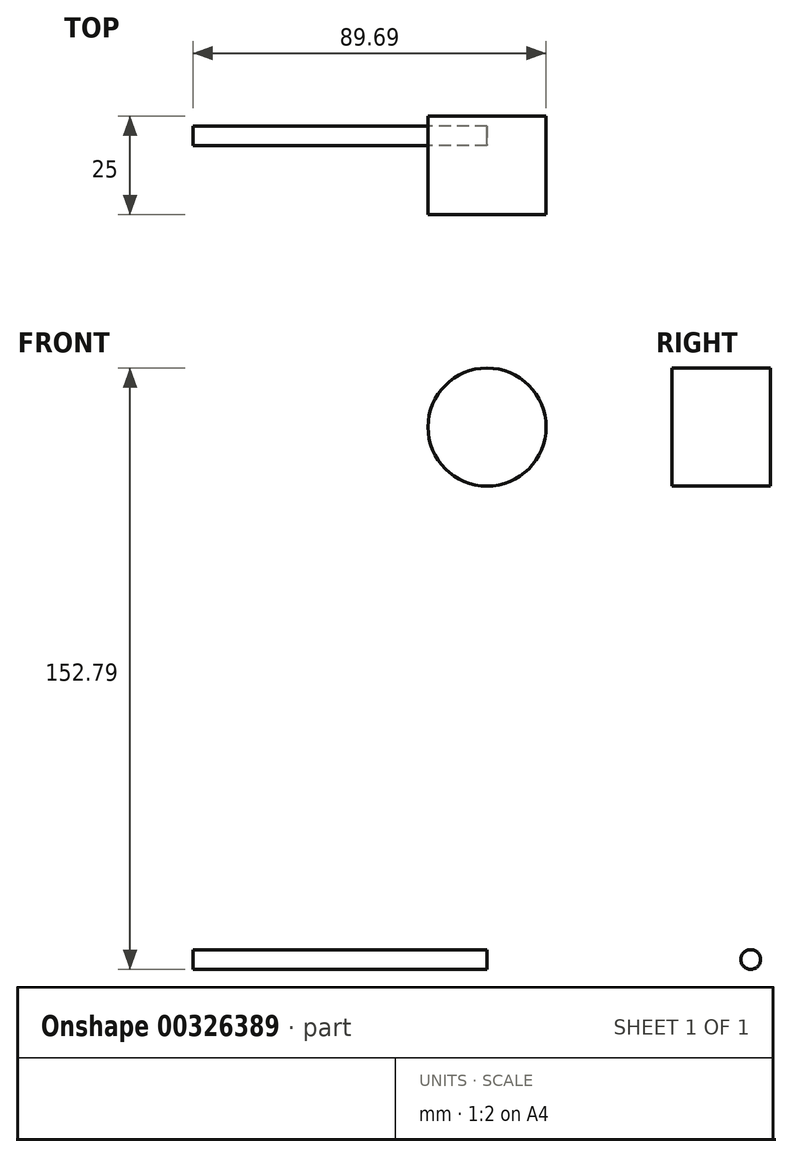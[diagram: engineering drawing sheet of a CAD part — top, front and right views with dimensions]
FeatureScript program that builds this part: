
annotation { "Feature Type Name" : "Feature", "Feature Type Description" : "" }
export const myFeature = defineFeature(function(context is Context, id is Id, definition is map)
    precondition{}
    {
        {
            var Q0;
            Q0=qCreatedBy(makeId("Front.planeOp"),FACE);
            var sketch = newSketch(context, id + "F0", { "sketchPlane" : qUnion([Q0])});
            skLineSegment(sketch, "E0", {"start": v(100, 0) * mm, "end": v(25.31, 0) * mm});
            skCircle(sketch, "E1", {"center": v(100, 135.29) * mm, "radius": 15 * mm});
            skLineSegment(sketch, "E2", {"start": v(80, 135.29) * mm, "end": v(85, 135.29) * mm});
            skLineSegment(sketch, "E3", {"start": v(12.16, 22.2) * mm, "end": v(71.23, 130.1) * mm});
            skLineSegment(sketch, "E4", {"start": v(100, 135.29) * mm, "end": v(100, -96.08) * mm, "construction": true});
            skLineSegment(sketch, "E5", {"start": v(97.07, 150) * mm, "end": v(196.34, 150) * mm, "construction": true});
            skPoint(sketch, "E6.visualSharp", {"position": v(0, 0) * mm});
            skArc(sketch, "E6.filletArc", {"start": v(12.16, 22.2) * mm, "mid": v(12.4, 7.35) * mm, "end": v(25.31, 0) * mm});
            skPoint(sketch, "E7.visualSharp", {"position": v(74.07, 135.29) * mm});
            skArc(sketch, "E7.filletArc", {"start": v(80, 135.29) * mm, "mid": v(74.9, 133.9) * mm, "end": v(71.23, 130.1) * mm});
            skSolve(sketch);
        }
        {
            var Q0;
            Q0=qCreatedBy(makeId("Right.planeOp"),FACE);
            var Q1;
            Q1=sQuery(id+"F0.wireOp",VERTEX,"E0.start");
            cPlane(context, id + "F1", {"entities" : qUnion([Q0, Q1]), "cplaneType" : CPlaneType.PLANE_POINT, "offset" : 25 * mm, "width" : 150 * mm, "height" : 150 * mm});
        }
        {
            var Q0;
            Q0=qCreatedBy(id+"F1.planeOp",FACE);
            var sketch = newSketch(context, id + "F2", { "sketchPlane" : qUnion([Q0])});
            skCircle(sketch, "E8", {"center": v(0, 0) * mm, "radius": 2.5 * mm});
            skSolve(sketch);
        }
        {
            var Q0;
            Q0=qCreatedBy(makeId("Front.planeOp"),FACE);
            var sketch = newSketch(context, id + "F3", { "sketchPlane" : qUnion([Q0])});
            skLineSegment(sketch, "E9.0", {"start": v(100, 0) * mm, "end": v(25.31, 0) * mm});
            skSolve(sketch);
        }
        {
            var Q0;
            Q0 = qSketchRegion(id + "F2", true);
            var Q1;
            Q1 = qConstructionFilter(qBodyType(qCreatedBy(id + "F3" ,EDGE), BodyType.WIRE), ConstructionObject.NO);
            sweep(context, id + "F4", {"profiles" : qUnion([Q0]), "path" : qUnion([Q1])});
        }
        {
            var Q0;
            Q0=makeQuery(id+"F4.opSweep","CAP_FACE",FACE,{"disambiguationData":[OSD([sQuery(id+"F2.wireOp",EDGE,"E8"),sQuery(id+"F3.wireOp",VERTEX,"E9.0.end")])],"isStart":false});
            var sketch = newSketch(context, id + "F5", { "sketchPlane" : qUnion([Q0])});
            skCircle(sketch, "E10.0", {"center": v(0, 0) * mm, "radius": 2.5 * mm});
            skSolve(sketch);
        }
        {
            var Q0;
            Q0=qCreatedBy(makeId("Front.planeOp"),FACE);
            var sketch = newSketch(context, id + "F6", { "sketchPlane" : qUnion([Q0])});
            skArc(sketch, "E11.0", {"start": v(12.16, 22.2) * mm, "mid": v(12.4, 7.35) * mm, "end": v(25.31, 0) * mm});
            skLineSegment(sketch, "E12.0", {"start": v(12.16, 22.2) * mm, "end": v(71.23, 130.1) * mm});
            skArc(sketch, "E13.0", {"start": v(80, 135.29) * mm, "mid": v(74.9, 133.9) * mm, "end": v(71.23, 130.1) * mm});
            skLineSegment(sketch, "E14.0", {"start": v(80, 135.29) * mm, "end": v(85, 135.29) * mm});
            skLineSegment(sketch, "E15", {"start": v(85, 135.29) * mm, "end": v(93.11, 135.29) * mm});
            skSolve(sketch);
        }
        {
            var Q0;
            Q0=qCreatedBy(makeId("Front.planeOp"),FACE);
            var sketch = newSketch(context, id + "F7", { "sketchPlane" : qUnion([Q0])});
            skCircle(sketch, "E16.0", {"center": v(100, 135.29) * mm, "radius": 15 * mm});
            skSolve(sketch);
        }
        {
            var Q0;
            Q0 = qSketchRegion(id + "F7", true);
            extrude(context, id + "F8", {"entities" : qUnion([Q0]), "depth" : 20 * mm});
        }
        {
            var Q0;
            Q0=makeQuery(id+"F0.imprint","IMPRINT",FACE,{"disambiguationData":[TD([[makeQuery(id+"F0.imprint","IMPRINT",EDGE,{"derivedFrom":sQuery(id+"F0.wireOp",EDGE,"E1")}),1.0]])]});
            var sketch = newSketch(context, id + "F9", { "sketchPlane" : qUnion([Q0])});
            skCircle(sketch, "E17.0", {"center": v(100, 135.29) * mm, "radius": 15 * mm});
            skSolve(sketch);
        }
        {
            var Q0;
            Q0 = qSketchRegion(id + "F9", true);
            extrude(context, id + "F10", {"entities" : qUnion([Q0]), "operationType" : NewBodyOperationType.ADD, "oppositeDirection" : true, "depth" : 5 * mm});
        }
    });
